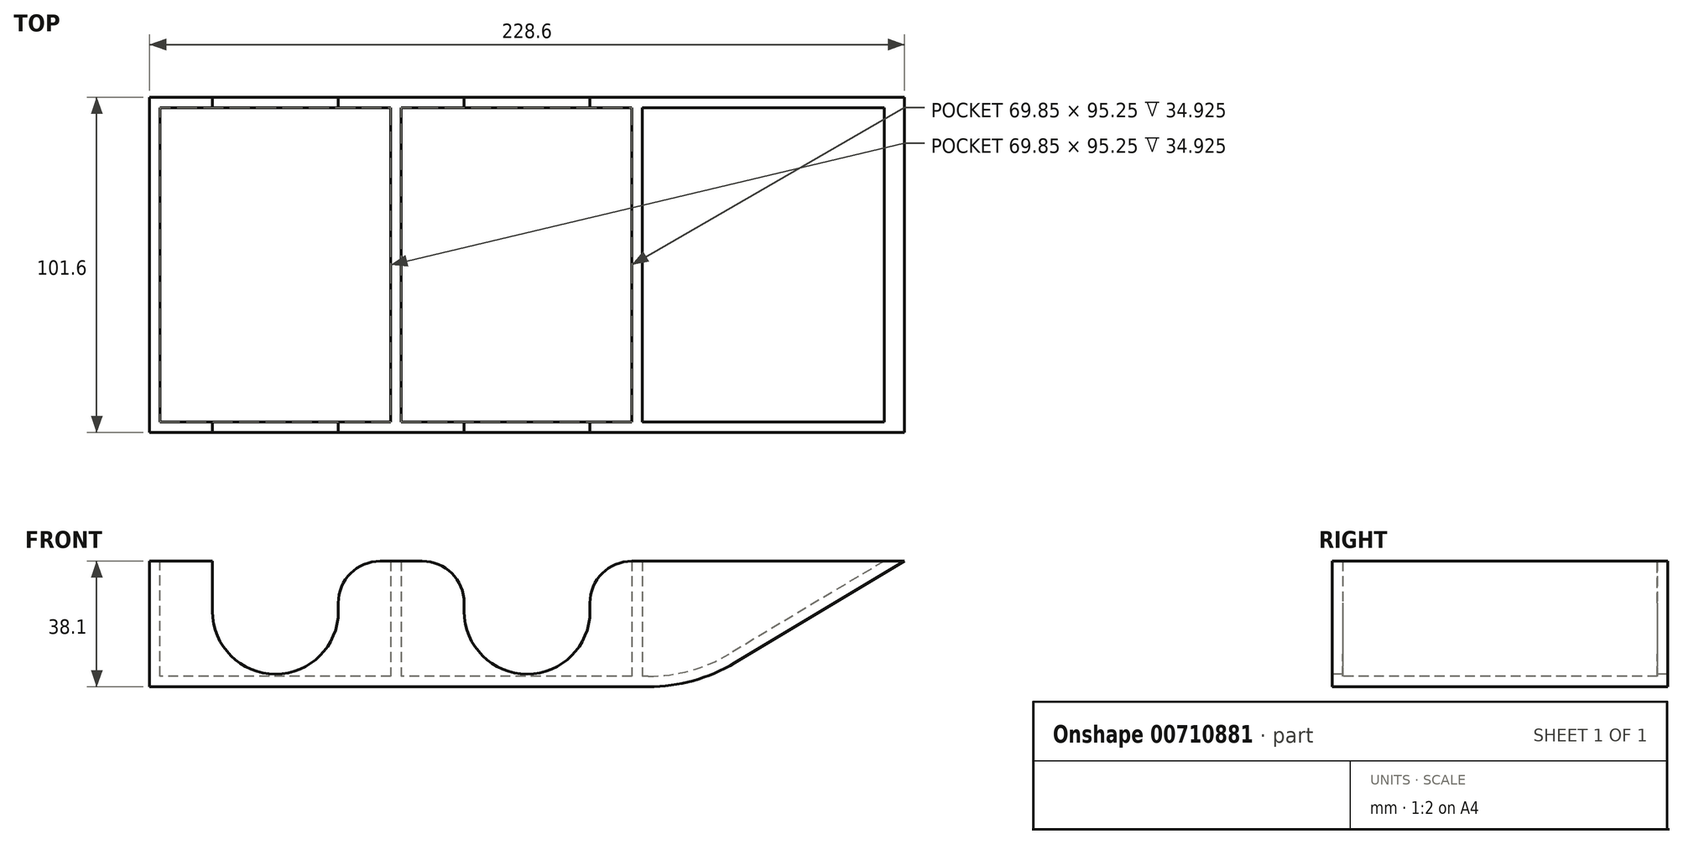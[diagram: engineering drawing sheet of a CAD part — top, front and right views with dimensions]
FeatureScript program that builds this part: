
annotation { "Feature Type Name" : "Feature", "Feature Type Description" : "" }
export const myFeature = defineFeature(function(context is Context, id is Id, definition is map)
    precondition{}
    {
        {
            var Q0;
            Q0=qCreatedBy(makeId("Front.planeOp"),FACE);
            var sketch = newSketch(context, id + "F0", { "sketchPlane" : qUnion([Q0])});
            skLineSegment(sketch, "E0", {"start": v(0, 0) * mm, "end": v(0, 38.1) * mm});
            skLineSegment(sketch, "E1", {"start": v(0, 38.1) * mm, "end": v(228.6, 38.1) * mm});
            skLineSegment(sketch, "E2", {"start": v(228.6, 38.1) * mm, "end": v(165.1, 0) * mm});
            skLineSegment(sketch, "E3", {"start": v(165.1, 0) * mm, "end": v(0, 0) * mm});
            skSolve(sketch);
        }
        {
            var Q0;
            Q0 = qSketchRegion(id + "F0", true);
            extrude(context, id + "F1", {"entities" : qUnion([Q0]), "depth" : 101.6 * mm, "offsetDistance" : 25.4 * mm});
        }
        {
            var Q0;
            Q0=makeQuery(id+"F1.opExtrude","SWEPT_EDGE",EDGE,{"disambiguationData":[OSD([sQuery(id+"F0.wireOp",EDGE,"E2"),sQuery(id+"F0.wireOp",EDGE,"E3")])]});
            fillet(context, id + "F2", {"entities" : qUnion([Q0]), "radius" : 50.8 * mm, "tangentPropagation" : true, "allowEdgeOverflow" : false});
        }
        {
            var Q0;
            Q0=makeQuery(id+"F1.opExtrude","SWEPT_FACE",FACE,{"disambiguationData":[OSD([sQuery(id+"F0.wireOp",EDGE,"E1")])]});
            shell(context, id + "F3", {"entities" : qUnion([Q0]), "thickness" : 3.17 * mm});
        }
        {
            var Q0;
            Q0=makeQuery(id+"F3.opShell","OFFSET_FACE",FACE,{"disambiguationData":[OSD([sQuery(id+"F0.wireOp",EDGE,"E3")])]});
            var sketch = newSketch(context, id + "F4", { "sketchPlane" : qUnion([Q0])});
            skLineSegment(sketch, "E4.bottom", {"start": v(73.03, -3.17) * mm, "end": v(76.2, -3.17) * mm});
            skLineSegment(sketch, "E4.top", {"start": v(73.03, -98.43) * mm, "end": v(76.2, -98.43) * mm});
            skLineSegment(sketch, "E4.left", {"start": v(73.03, -3.17) * mm, "end": v(73.03, -98.42) * mm});
            skLineSegment(sketch, "E4.right", {"start": v(76.2, -3.17) * mm, "end": v(76.2, -98.43) * mm});
            skLineSegment(sketch, "E5.bottom", {"start": v(146.05, -3.17) * mm, "end": v(149.23, -3.17) * mm});
            skLineSegment(sketch, "E5.top", {"start": v(146.05, -98.43) * mm, "end": v(149.23, -98.43) * mm});
            skLineSegment(sketch, "E5.left", {"start": v(146.05, -3.17) * mm, "end": v(146.05, -98.43) * mm});
            skLineSegment(sketch, "E5.right", {"start": v(149.23, -3.17) * mm, "end": v(149.23, -98.43) * mm});
            skSolve(sketch);
        }
        {
            var Q0;
            Q0 = qSketchRegion(id + "F4", true);
            var Q1;
            Q1=makeQuery(id+"F1.opExtrude","SWEPT_FACE",FACE,{"disambiguationData":[OSD([sQuery(id+"F0.wireOp",EDGE,"E1")])]});
            extrude(context, id + "F5", {"entities" : qUnion([Q0]), "operationType" : NewBodyOperationType.ADD, "endBound" : BoundingType.UP_TO_SURFACE, "depth" : 25.4 * mm, "endBoundEntityFace" : qUnion([Q1]), "offsetDistance" : 25.4 * mm});
        }
        {
            var Q0;
            Q0=makeQuery(id+"F1.opExtrude","CAP_FACE",FACE,{"disambiguationData":[OSD([sQuery(id+"F0.wireOp",EDGE,"E0"),sQuery(id+"F0.wireOp",EDGE,"E1"),sQuery(id+"F0.wireOp",EDGE,"E2"),sQuery(id+"F0.wireOp",EDGE,"E3")])],"isStart":false});
            var sketch = newSketch(context, id + "F6", { "sketchPlane" : qUnion([Q0])});
            skLineSegment(sketch, "E6", {"start": v(19.05, 38.1) * mm, "end": v(19.05, 22.86) * mm});
            skLineSegment(sketch, "E7", {"start": v(57.15, 38.1) * mm, "end": v(57.15, 22.86) * mm});
            skArc(sketch, "E8", {"start": v(19.05, 22.86) * mm, "mid": v(38.1, 3.81) * mm, "end": v(57.15, 22.86) * mm});
            skLineSegment(sketch, "E9", {"start": v(19.05, 38.1) * mm, "end": v(57.15, 38.1) * mm});
            skLineSegment(sketch, "E10.1.0.0", {"start": v(95.25, 38.1) * mm, "end": v(133.35, 38.1) * mm});
            skLineSegment(sketch, "E10.1.0.1", {"start": v(95.25, 38.1) * mm, "end": v(95.25, 22.86) * mm});
            skArc(sketch, "E10.1.0.2", {"start": v(95.25, 22.86) * mm, "mid": v(114.3, 3.81) * mm, "end": v(133.35, 22.86) * mm});
            skLineSegment(sketch, "E10.1.0.3", {"start": v(133.35, 38.1) * mm, "end": v(133.35, 22.86) * mm});
            skLineSegment(sketch, "E10.direction1", {"start": v(19.05, 38.1) * mm, "end": v(95.25, 38.1) * mm, "construction": true});
            skSolve(sketch);
        }
        {
            var Q0;
            Q0 = qSketchRegion(id + "F6", true);
            extrude(context, id + "F7", {"entities" : qUnion([Q0]), "operationType" : NewBodyOperationType.REMOVE, "endBound" : BoundingType.THROUGH_ALL, "oppositeDirection" : true, "depth" : 25.4 * mm, "offsetDistance" : 25.4 * mm});
        }
        {
            var Q0;
            {var subQ0=sQuery(id+"F0.wireOp",EDGE,"E1");var subQ1=sQuery(id+"F0.wireOp",EDGE,"E3");var subQ2=sQuery(id+"F0.wireOp",EDGE,"E2");var subQ3=sQuery(id+"F0.wireOp",EDGE,"E0");var subQ4=makeQuery(id+"F1.opExtrude","CAP_FACE",FACE,{"disambiguationData":[OSD([subQ3,subQ0,subQ2,subQ1])],"isStart":false});var subQ5=sQuery(id+"F6.wireOp",EDGE,"E6");Q0=makeQuery(id+"F7.boolean.opBoolean","COPY",EDGE,{"disambiguationData":[TD([subQ4])],"derivedFrom":makeQuery(id+"F7.opExtrude","SWEPT_EDGE",EDGE,{"disambiguationData":[OSD([subQ0,subQ5,sQuery(id+"F6.wireOp",EDGE,"E9")])]})});}
            var Q1;
            {var subQ0=sQuery(id+"F0.wireOp",EDGE,"E1");var subQ1=sQuery(id+"F0.wireOp",EDGE,"E3");var subQ2=sQuery(id+"F0.wireOp",EDGE,"E2");var subQ3=sQuery(id+"F0.wireOp",EDGE,"E0");var subQ4=makeQuery(id+"F1.opExtrude","CAP_FACE",FACE,{"disambiguationData":[OSD([subQ3,subQ0,subQ2,subQ1])],"isStart":false});var subQ5=sQuery(id+"F6.wireOp",EDGE,"E7");Q1=makeQuery(id+"F7.boolean.opBoolean","COPY",EDGE,{"disambiguationData":[TD([subQ4])],"derivedFrom":makeQuery(id+"F7.opExtrude","SWEPT_EDGE",EDGE,{"disambiguationData":[OSD([subQ0,subQ5,sQuery(id+"F6.wireOp",EDGE,"E9")])]})});}
            var Q2;
            {var subQ0=sQuery(id+"F0.wireOp",EDGE,"E1");var subQ1=sQuery(id+"F0.wireOp",EDGE,"E3");var subQ2=sQuery(id+"F0.wireOp",EDGE,"E2");var subQ3=sQuery(id+"F0.wireOp",EDGE,"E0");var subQ4=makeQuery(id+"F1.opExtrude","CAP_FACE",FACE,{"disambiguationData":[OSD([subQ3,subQ0,subQ2,subQ1])],"isStart":true});var subQ5=sQuery(id+"F6.wireOp",EDGE,"E6");Q2=makeQuery(id+"F7.boolean.opBoolean","COPY",EDGE,{"disambiguationData":[TD([subQ4])],"derivedFrom":makeQuery(id+"F7.opExtrude","SWEPT_EDGE",EDGE,{"disambiguationData":[OSD([subQ0,subQ5,sQuery(id+"F6.wireOp",EDGE,"E9")])]})});}
            var Q3;
            {var subQ0=sQuery(id+"F0.wireOp",EDGE,"E1");var subQ1=sQuery(id+"F0.wireOp",EDGE,"E3");var subQ2=sQuery(id+"F0.wireOp",EDGE,"E2");var subQ3=sQuery(id+"F0.wireOp",EDGE,"E0");var subQ4=makeQuery(id+"F1.opExtrude","CAP_FACE",FACE,{"disambiguationData":[OSD([subQ3,subQ0,subQ2,subQ1])],"isStart":true});var subQ5=sQuery(id+"F6.wireOp",EDGE,"E7");Q3=makeQuery(id+"F7.boolean.opBoolean","COPY",EDGE,{"disambiguationData":[TD([subQ4])],"derivedFrom":makeQuery(id+"F7.opExtrude","SWEPT_EDGE",EDGE,{"disambiguationData":[OSD([subQ0,subQ5,sQuery(id+"F6.wireOp",EDGE,"E9")])]})});}
            var Q4;
            {var subQ0=sQuery(id+"F0.wireOp",EDGE,"E1");var subQ1=sQuery(id+"F0.wireOp",EDGE,"E3");var subQ2=sQuery(id+"F0.wireOp",EDGE,"E2");var subQ3=sQuery(id+"F0.wireOp",EDGE,"E0");var subQ4=makeQuery(id+"F1.opExtrude","CAP_FACE",FACE,{"disambiguationData":[OSD([subQ3,subQ0,subQ2,subQ1])],"isStart":false});var subQ5=sQuery(id+"F6.wireOp",EDGE,"E10.1.0.1");Q4=makeQuery(id+"F7.boolean.opBoolean","COPY",EDGE,{"disambiguationData":[TD([subQ4])],"derivedFrom":makeQuery(id+"F7.opExtrude","SWEPT_EDGE",EDGE,{"disambiguationData":[OSD([subQ0,sQuery(id+"F6.wireOp",EDGE,"E10.1.0.0"),subQ5])]})});}
            var Q5;
            {var subQ0=sQuery(id+"F0.wireOp",EDGE,"E1");var subQ1=sQuery(id+"F0.wireOp",EDGE,"E3");var subQ2=sQuery(id+"F0.wireOp",EDGE,"E2");var subQ3=sQuery(id+"F0.wireOp",EDGE,"E0");var subQ4=makeQuery(id+"F1.opExtrude","CAP_FACE",FACE,{"disambiguationData":[OSD([subQ3,subQ0,subQ2,subQ1])],"isStart":false});var subQ5=sQuery(id+"F6.wireOp",EDGE,"E10.1.0.3");Q5=makeQuery(id+"F7.boolean.opBoolean","COPY",EDGE,{"disambiguationData":[TD([subQ4])],"derivedFrom":makeQuery(id+"F7.opExtrude","SWEPT_EDGE",EDGE,{"disambiguationData":[OSD([subQ0,sQuery(id+"F6.wireOp",EDGE,"E10.1.0.0"),subQ5])]})});}
            var Q6;
            {var subQ0=sQuery(id+"F0.wireOp",EDGE,"E1");var subQ1=sQuery(id+"F0.wireOp",EDGE,"E3");var subQ2=sQuery(id+"F0.wireOp",EDGE,"E2");var subQ3=sQuery(id+"F0.wireOp",EDGE,"E0");var subQ4=makeQuery(id+"F1.opExtrude","CAP_FACE",FACE,{"disambiguationData":[OSD([subQ3,subQ0,subQ2,subQ1])],"isStart":true});var subQ5=sQuery(id+"F6.wireOp",EDGE,"E10.1.0.3");Q6=makeQuery(id+"F7.boolean.opBoolean","COPY",EDGE,{"disambiguationData":[TD([subQ4])],"derivedFrom":makeQuery(id+"F7.opExtrude","SWEPT_EDGE",EDGE,{"disambiguationData":[OSD([subQ0,sQuery(id+"F6.wireOp",EDGE,"E10.1.0.0"),subQ5])]})});}
            var Q7;
            {var subQ0=sQuery(id+"F0.wireOp",EDGE,"E1");var subQ1=sQuery(id+"F0.wireOp",EDGE,"E3");var subQ2=sQuery(id+"F0.wireOp",EDGE,"E2");var subQ3=sQuery(id+"F0.wireOp",EDGE,"E0");var subQ4=makeQuery(id+"F1.opExtrude","CAP_FACE",FACE,{"disambiguationData":[OSD([subQ3,subQ0,subQ2,subQ1])],"isStart":true});var subQ5=sQuery(id+"F6.wireOp",EDGE,"E10.1.0.1");Q7=makeQuery(id+"F7.boolean.opBoolean","COPY",EDGE,{"disambiguationData":[TD([subQ4])],"derivedFrom":makeQuery(id+"F7.opExtrude","SWEPT_EDGE",EDGE,{"disambiguationData":[OSD([subQ0,sQuery(id+"F6.wireOp",EDGE,"E10.1.0.0"),subQ5])]})});}
            fillet(context, id + "F8", {"entities" : qUnion([Q0, Q1, Q2, Q3, Q4, Q5, Q6, Q7]), "radius" : 12.7 * mm, "tangentPropagation" : true, "allowEdgeOverflow" : false});
        }
    });
